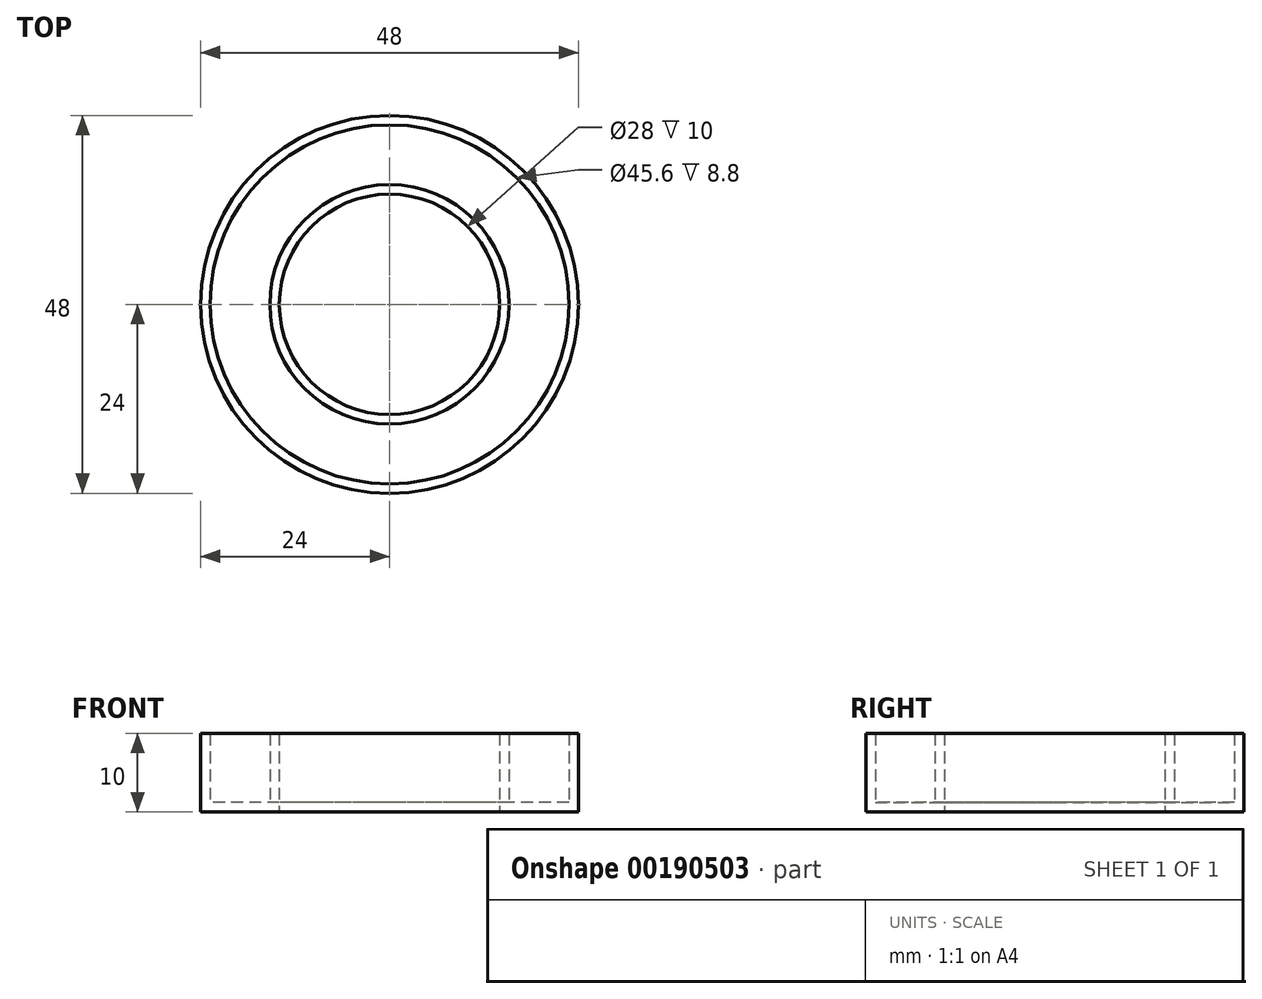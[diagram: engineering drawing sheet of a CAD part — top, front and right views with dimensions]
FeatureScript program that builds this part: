
annotation { "Feature Type Name" : "Feature", "Feature Type Description" : "" }
export const myFeature = defineFeature(function(context is Context, id is Id, definition is map)
    precondition{}
    {
        {
            var Q0;
            Q0=qCreatedBy(makeId("Top.planeOp"),FACE);
            var sketch = newSketch(context, id + "F0", { "sketchPlane" : qUnion([Q0])});
            skCircle(sketch, "E0", {"center": v(0, 0) * mm, "radius": 14 * mm});
            skCircle(sketch, "E1", {"center": v(0, 0) * mm, "radius": 24 * mm});
            skSolve(sketch);
        }
        {
            var Q0;
            Q0 = qSketchRegion(id + "F0", true);
            extrude(context, id + "F1", {"entities" : qUnion([Q0]), "depth" : 10 * mm});
        }
        {
            var Q0;
            Q0=makeQuery(id+"F1.opExtrude","CAP_FACE",FACE,{"disambiguationData":[OSD([sQuery(id+"F0.wireOp",EDGE,"E0"),sQuery(id+"F0.wireOp",EDGE,"E1")])],"isStart":false});
            shell(context, id + "F2", {"entities" : qUnion([Q0]), "thickness" : 1.2 * mm});
        }
    });
